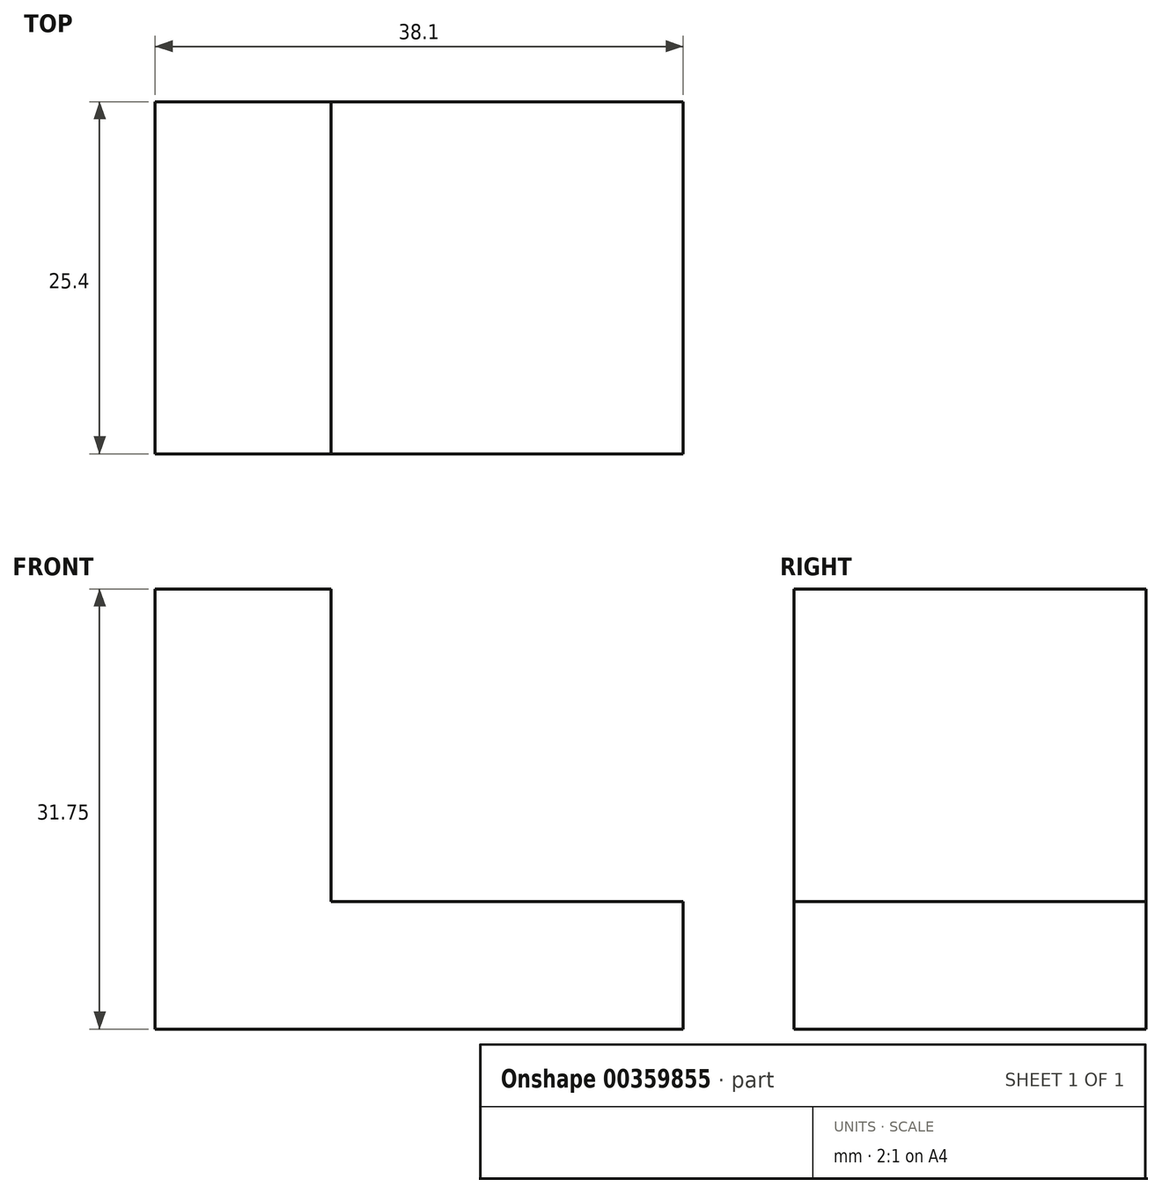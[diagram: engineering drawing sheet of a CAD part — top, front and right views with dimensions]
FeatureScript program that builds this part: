
annotation { "Feature Type Name" : "Feature", "Feature Type Description" : "" }
export const myFeature = defineFeature(function(context is Context, id is Id, definition is map)
    precondition{}
    {
        {
            var Q0;
            Q0=qCreatedBy(makeId("Front.planeOp"),FACE);
            var sketch = newSketch(context, id + "F0", { "sketchPlane" : qUnion([Q0])});
            skLineSegment(sketch, "E0", {"start": v(0, 0) * mm, "end": v(38.1, 0) * mm});
            skLineSegment(sketch, "E1", {"start": v(38.1, 0) * mm, "end": v(38.1, 9.2) * mm});
            skLineSegment(sketch, "E2", {"start": v(38.1, 9.2) * mm, "end": v(12.7, 9.2) * mm});
            skLineSegment(sketch, "E3", {"start": v(12.7, 9.2) * mm, "end": v(12.7, 31.75) * mm});
            skLineSegment(sketch, "E4", {"start": v(12.7, 31.75) * mm, "end": v(0, 31.75) * mm});
            skLineSegment(sketch, "E5", {"start": v(0, 31.75) * mm, "end": v(0, 0) * mm});
            skSolve(sketch);
        }
        {
            var Q0;
            Q0 = qSketchRegion(id + "F0", true);
            extrude(context, id + "F1", {"entities" : qUnion([Q0]), "depth" : 25.4 * mm});
        }
    });
